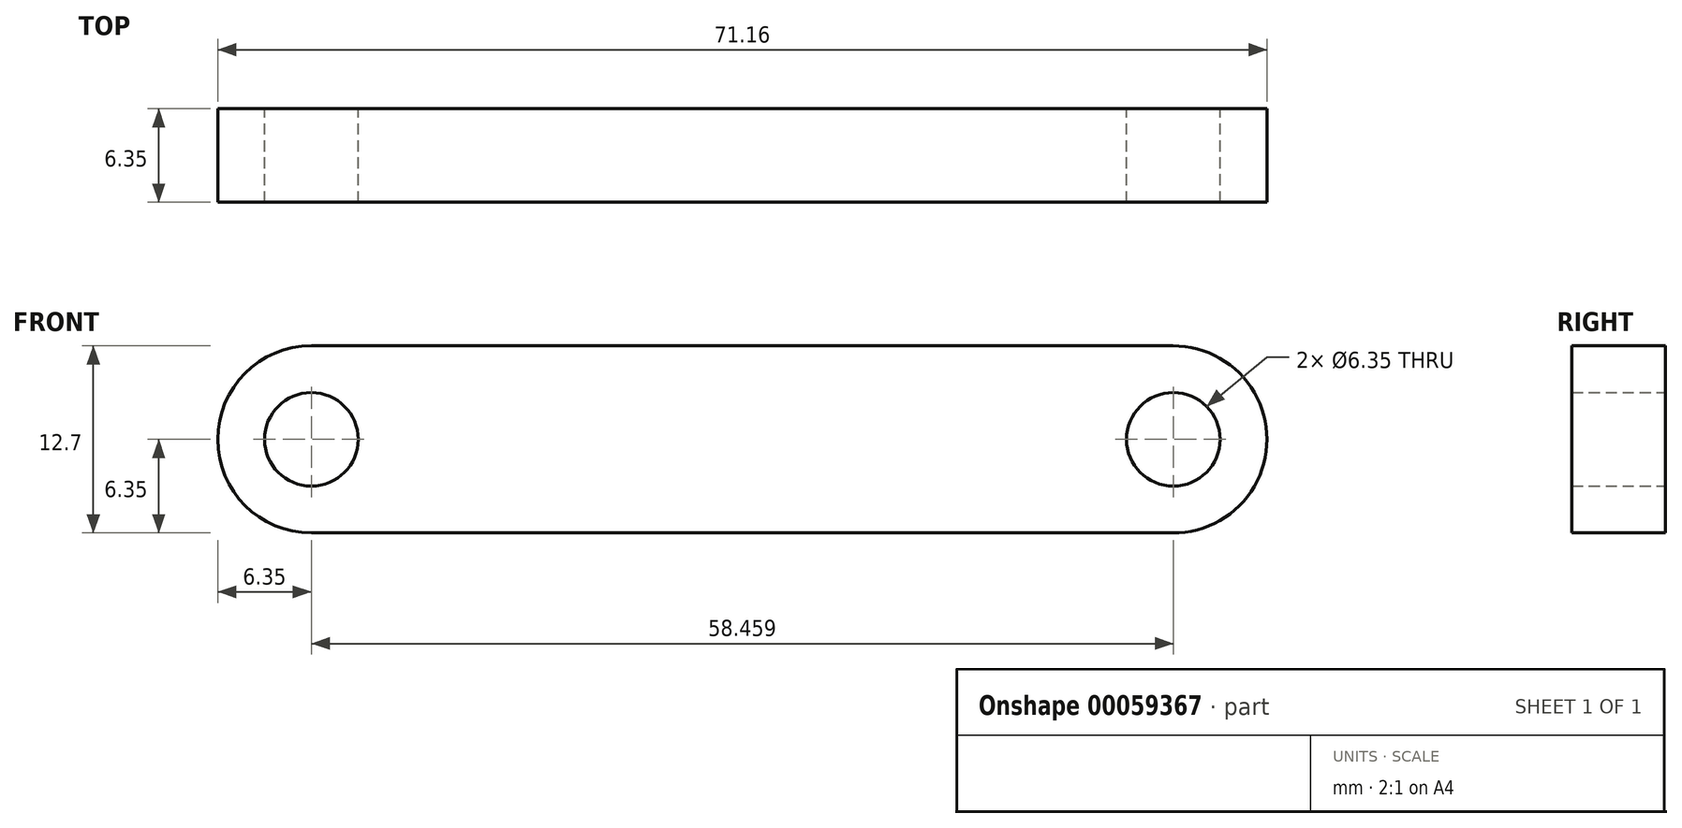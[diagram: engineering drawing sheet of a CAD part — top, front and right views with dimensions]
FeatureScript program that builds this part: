
annotation { "Feature Type Name" : "Feature", "Feature Type Description" : "" }
export const myFeature = defineFeature(function(context is Context, id is Id, definition is map)
    precondition{}
    {
        {
            var Q0;
            Q0=qCreatedBy(makeId("Front.planeOp"),FACE);
            var sketch = newSketch(context, id + "F0", { "sketchPlane" : qUnion([Q0])});
            skLineSegment(sketch, "E0.bottom", {"start": v(-29.2, 6.35) * mm, "end": v(29.21, 6.35) * mm});
            skLineSegment(sketch, "E0.top", {"start": v(-29.2, -6.35) * mm, "end": v(29.21, -6.35) * mm});
            skLineSegment(sketch, "E1", {"start": v(-38.07, 0) * mm, "end": v(42.54, 0) * mm, "construction": true});
            skLineSegment(sketch, "E2", {"start": v(0, 31.57) * mm, "end": v(0, -25.93) * mm, "construction": true});
            skCircle(sketch, "E3", {"center": v(-29.21, 0) * mm, "radius": 3.18 * mm});
            skCircle(sketch, "E4", {"center": v(29.25, 0) * mm, "radius": 3.18 * mm});
            skArc(sketch, "E5", {"start": v(-29.2, 6.35) * mm, "mid": v(-35.56, 0) * mm, "end": v(-29.2, -6.35) * mm});
            skArc(sketch, "E6", {"start": v(29.21, -6.35) * mm, "mid": v(35.6, 0) * mm, "end": v(29.21, 6.35) * mm});
            skSolve(sketch);
        }
        {
            var Q0;
            Q0=makeQuery(id+"F0.imprint","IMPRINT",FACE,{"disambiguationData":[TD([[makeQuery(id+"F0.imprint","IMPRINT",EDGE,{"derivedFrom":sQuery(id+"F0.wireOp",EDGE,"E0.bottom")}),-1.0]])]});
            extrude(context, id + "F1", {"entities" : qUnion([Q0]), "depth" : 6.35 * mm});
        }
    });
